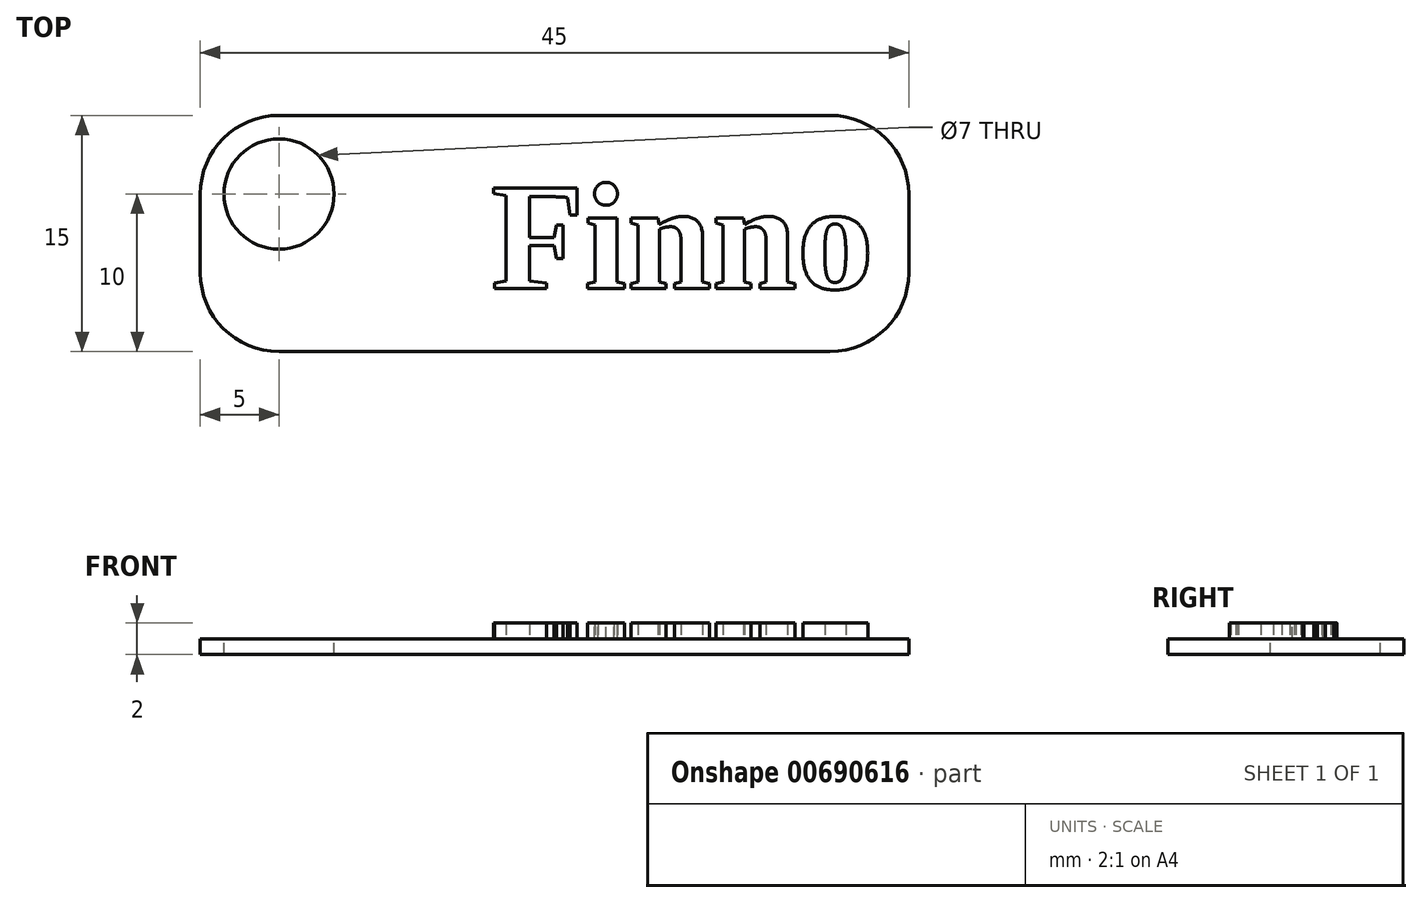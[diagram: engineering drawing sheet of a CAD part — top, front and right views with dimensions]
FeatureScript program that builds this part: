
annotation { "Feature Type Name" : "Feature", "Feature Type Description" : "" }
export const myFeature = defineFeature(function(context is Context, id is Id, definition is map)
    precondition{}
    {
        {
            var Q0;
            Q0=qCreatedBy(makeId("Top.planeOp"),FACE);
            var sketch = newSketch(context, id + "F0", { "sketchPlane" : qUnion([Q0])});
            skLineSegment(sketch, "E0.bottom", {"start": v(22.5, -7.5) * mm, "end": v(-22.5, -7.5) * mm});
            skLineSegment(sketch, "E0.top", {"start": v(22.5, 7.5) * mm, "end": v(-22.5, 7.5) * mm});
            skLineSegment(sketch, "E0.left", {"start": v(22.5, -7.5) * mm, "end": v(22.5, 7.5) * mm});
            skLineSegment(sketch, "E0.right", {"start": v(-22.5, -7.5) * mm, "end": v(-22.5, 7.5) * mm});
            skPoint(sketch, "E0.middle", {"position": v(0, 0) * mm});
            skSolve(sketch);
        }
        {
            var Q0;
            Q0 = qSketchRegion(id + "F0", true);
            extrude(context, id + "F1", {"entities" : qUnion([Q0]), "depth" : 1 * mm, "offsetDistance" : 25 * mm});
        }
        {
            var Q0;
            Q0=makeQuery(id+"F1.opExtrude","SWEPT_EDGE",EDGE,{"disambiguationData":[OSD([sQuery(id+"F0.wireOp",EDGE,"E0.bottom"),sQuery(id+"F0.wireOp",EDGE,"E0.right")])]});
            var Q1;
            Q1=makeQuery(id+"F1.opExtrude","SWEPT_EDGE",EDGE,{"disambiguationData":[OSD([sQuery(id+"F0.wireOp",EDGE,"E0.bottom"),sQuery(id+"F0.wireOp",EDGE,"E0.left")])]});
            var Q2;
            Q2=makeQuery(id+"F1.opExtrude","SWEPT_EDGE",EDGE,{"disambiguationData":[OSD([sQuery(id+"F0.wireOp",EDGE,"E0.top"),sQuery(id+"F0.wireOp",EDGE,"E0.left")])]});
            var Q3;
            Q3=makeQuery(id+"F1.opExtrude","SWEPT_EDGE",EDGE,{"disambiguationData":[OSD([sQuery(id+"F0.wireOp",EDGE,"E0.top"),sQuery(id+"F0.wireOp",EDGE,"E0.right")])]});
            fillet(context, id + "F2", {"entities" : qUnion([Q0, Q1, Q2, Q3]), "radius" : 5 * mm, "tangentPropagation" : true, "allowEdgeOverflow" : false});
        }
        {
            var Q0;
            Q0=makeQuery(id+"F1.opExtrude","CAP_FACE",FACE,{"disambiguationData":[OSD([sQuery(id+"F0.wireOp",EDGE,"E0.bottom"),sQuery(id+"F0.wireOp",EDGE,"E0.top"),sQuery(id+"F0.wireOp",EDGE,"E0.left"),sQuery(id+"F0.wireOp",EDGE,"E0.right")])],"isStart":false});
            var sketch = newSketch(context, id + "F3", { "sketchPlane" : qUnion([Q0])});
            skLineSegment(sketch, "E1", {"start": v(-17.5, 7.5) * mm, "end": v(-17.5, -7.5) * mm, "construction": true});
            skLineSegment(sketch, "E2", {"start": v(-17.5, -7.5) * mm, "end": v(0, 7.5) * mm, "construction": true});
            skLineSegment(sketch, "E3", {"start": v(0, 7.5) * mm, "end": v(17.5, -7.5) * mm, "construction": true});
            skLineSegment(sketch, "E4", {"start": v(17.5, -7.5) * mm, "end": v(17.5, 7.5) * mm, "construction": true});
            skLineSegment(sketch, "E5", {"start": v(17.5, 7.5) * mm, "end": v(0, -7.5) * mm, "construction": true});
            skLineSegment(sketch, "E6", {"start": v(0, -7.5) * mm, "end": v(-17.5, 7.5) * mm, "construction": true});
            skPoint(sketch, "E7", {"position": v(-17.5, 2.5) * mm});
            skSolve(sketch);
        }
        {
            var Q0;
            Q0=sQuery(id+"F3.wireOp",VERTEX,"E7");
            var Q1;
            Q1=makeQuery(id+"F1.opExtrude","SWEPT_BODY",BODY,{"disambiguationData":[OSD([sQuery(id+"F0.wireOp",EDGE,"E0.bottom"),sQuery(id+"F0.wireOp",EDGE,"E0.top"),sQuery(id+"F0.wireOp",EDGE,"E0.left"),sQuery(id+"F0.wireOp",EDGE,"E0.right")])]});
            hole(context, id + "F4", {"style" : HoleStyle.SIMPLE, "endStyle" : HoleEndStyle.BLIND, "holeDiameter" : 7 * mm, "majorDiameter" : 5 * mm, "holeDepth" : 15.5 * mm, "isTappedThrough" : true, "tappedDepth" : 12 * mm, "tapClearance" : 3, "locations" : qUnion([Q0]), "scope" : qUnion([Q1])});
        }
        {
            var Q0;
            Q0=makeQuery(id+"F1.opExtrude","CAP_FACE",FACE,{"disambiguationData":[OSD([sQuery(id+"F0.wireOp",EDGE,"E0.bottom"),sQuery(id+"F0.wireOp",EDGE,"E0.top"),sQuery(id+"F0.wireOp",EDGE,"E0.left"),sQuery(id+"F0.wireOp",EDGE,"E0.right")])],"isStart":false});
            var sketch = newSketch(context, id + "F5", { "sketchPlane" : qUnion([Q0])});
            skText(sketch, "E8", { "text": "Finno", "fontName": "Tinos-Bold.ttf"});
            const initialGuessF5  = {"E8": [-0.00405, -0.0035, 1, 0, 0.007]};
            skSetInitialGuess(sketch, initialGuessF5);
            skSolve(sketch);
        }
        {
            var Q0;
            Q0 = qSketchRegion(id + "F5", true);
            extrude(context, id + "F6", {"entities" : qUnion([Q0]), "operationType" : NewBodyOperationType.ADD, "depth" : 1 * mm, "offsetDistance" : 25 * mm});
        }
    });
